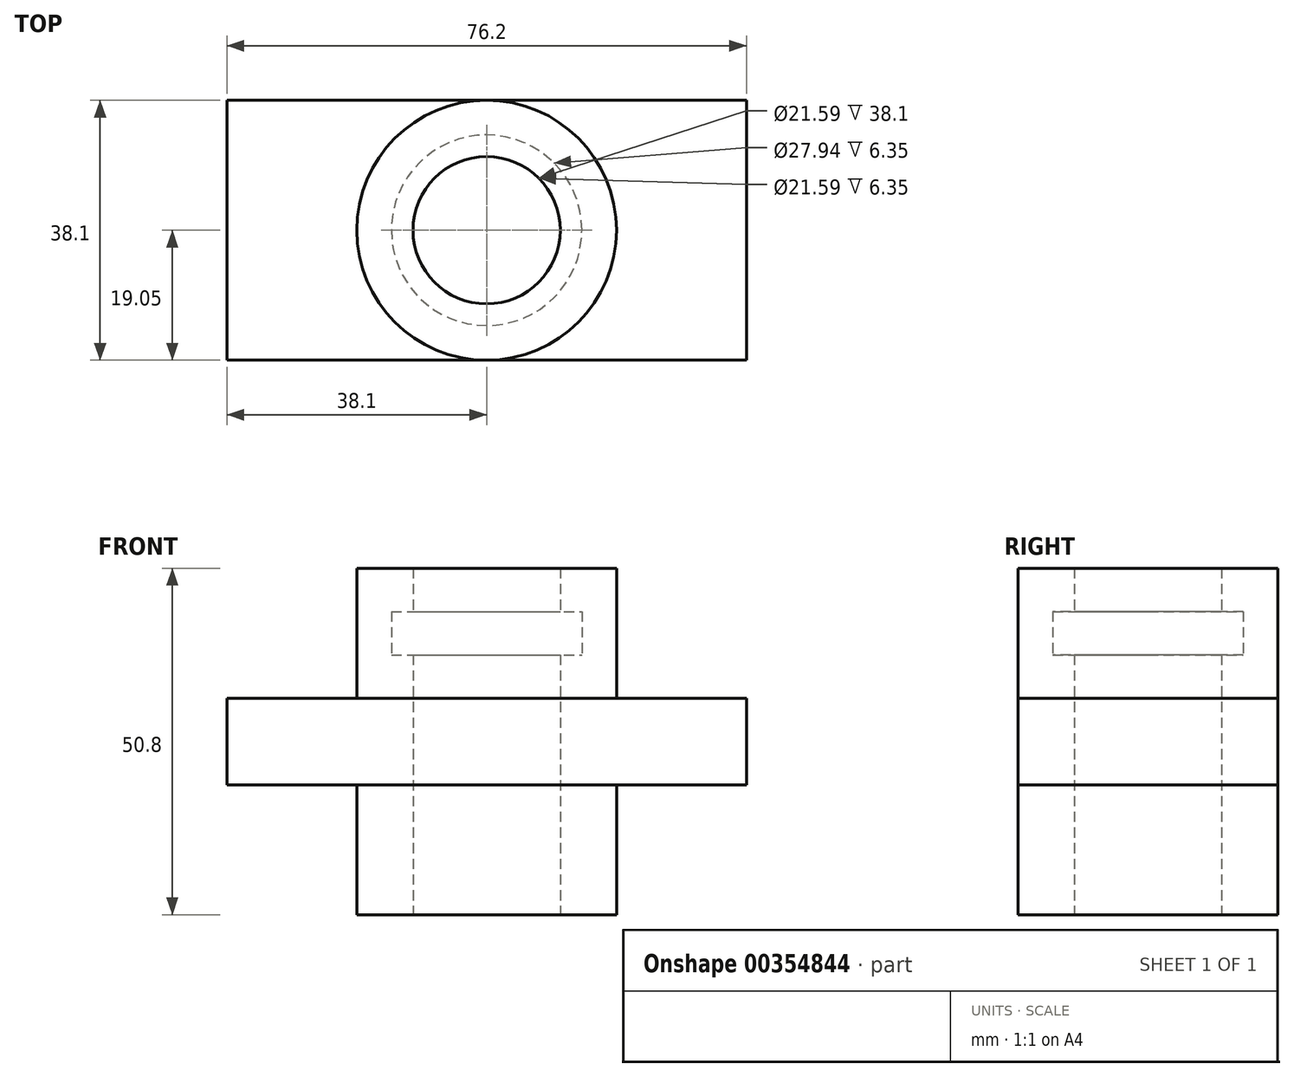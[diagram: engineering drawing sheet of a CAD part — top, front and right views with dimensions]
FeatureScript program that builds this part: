
annotation { "Feature Type Name" : "Feature", "Feature Type Description" : "" }
export const myFeature = defineFeature(function(context is Context, id is Id, definition is map)
    precondition{}
    {
        {
            var Q0;
            Q0=qCreatedBy(makeId("Front.planeOp"),FACE);
            var sketch = newSketch(context, id + "F0", { "sketchPlane" : qUnion([Q0])});
            skLineSegment(sketch, "E0", {"start": v(0, 0) * mm, "end": v(38.1, 0) * mm});
            skLineSegment(sketch, "E1", {"start": v(38.1, 0) * mm, "end": v(38.1, 12.7) * mm});
            skLineSegment(sketch, "E2", {"start": v(38.1, 12.7) * mm, "end": v(-38.1, 12.7) * mm});
            skLineSegment(sketch, "E3", {"start": v(-38.1, 12.7) * mm, "end": v(-38.1, 0) * mm});
            skLineSegment(sketch, "E4", {"start": v(-38.1, 0) * mm, "end": v(0, 0) * mm});
            skSolve(sketch);
        }
        {
            var Q0;
            Q0=makeQuery(id+"F0.imprint","IMPRINT",FACE,{"disambiguationData":[TD([[makeQuery(id+"F0.imprint","IMPRINT",EDGE,{"derivedFrom":sQuery(id+"F0.wireOp",EDGE,"E0")}),1.0]])]});
            extrude(context, id + "F1", {"entities" : qUnion([Q0]), "endBound" : BoundingType.SYMMETRIC, "depth" : 38.1 * mm});
        }
        {
            var Q0;
            Q0=qCreatedBy(makeId("Front.planeOp"),FACE);
            var sketch = newSketch(context, id + "F2", { "sketchPlane" : qUnion([Q0])});
            skLineSegment(sketch, "E5.0.0", {"start": v(-38.1, 12.7) * mm, "end": v(-38.1, 0) * mm});
            skLineSegment(sketch, "E5.0.1", {"start": v(-38.1, 0) * mm, "end": v(38.1, 0) * mm});
            skLineSegment(sketch, "E5.0.2", {"start": v(38.1, 0) * mm, "end": v(38.1, 12.7) * mm});
            skLineSegment(sketch, "E5.0.3", {"start": v(38.1, 12.7) * mm, "end": v(-38.1, 12.7) * mm});
            skLineSegment(sketch, "E6", {"start": v(0, 12.7) * mm, "end": v(-19.05, 12.7) * mm});
            skLineSegment(sketch, "E7", {"start": v(-19.05, 12.7) * mm, "end": v(-19.05, 31.75) * mm});
            skLineSegment(sketch, "E8", {"start": v(-19.05, 31.75) * mm, "end": v(-10.8, 31.75) * mm});
            skLineSegment(sketch, "E9", {"start": v(-10.8, 31.75) * mm, "end": v(-10.8, 25.4) * mm});
            skLineSegment(sketch, "E10", {"start": v(-10.8, 25.4) * mm, "end": v(-13.97, 25.4) * mm});
            skLineSegment(sketch, "E11", {"start": v(-13.97, 25.4) * mm, "end": v(-13.97, 19.05) * mm});
            skLineSegment(sketch, "E12", {"start": v(-13.97, 19.05) * mm, "end": v(-10.8, 19.05) * mm});
            skLineSegment(sketch, "E13", {"start": v(-10.8, 19.05) * mm, "end": v(-10.8, 12.7) * mm});
            skLineSegment(sketch, "E14", {"start": v(0, 12.7) * mm, "end": v(0, 18.62) * mm});
            skSolve(sketch);
        }
        {
            var Q0;
            {var subQ0=sQuery(id+"F2.wireOp",EDGE,"E7");Q0=makeQuery(id+"F2.imprint","IMPRINT",FACE,{"disambiguationData":[TD([[makeQuery(id+"F2.imprint","IMPRINT",EDGE,{"derivedFrom":subQ0}),-1.0]])]});}
            var Q1;
            Q1=sQuery(id+"F2.wireOp",EDGE,"E14");
            revolve(context, id + "F3", {"operationType" : NewBodyOperationType.ADD, "entities" : qUnion([Q0]), "axis" : qUnion([Q1]), "revolveType" : RevolveType.FULL});
        }
        {
            var Q0;
            Q0=makeQuery(id+"F3.boolean.opBoolean","SPLIT",FACE,{"disambiguationData":[TD([makeQuery(id+"F3.opRevolve","SWEPT_FACE",FACE,{"disambiguationData":[OSD([sQuery(id+"F2.wireOp",EDGE,"E13")])]})])],"derivedFrom":makeQuery(id+"F1.opExtrude","SWEPT_FACE",FACE,{"disambiguationData":[OSD([sQuery(id+"F0.wireOp",EDGE,"E2")])]})});
            extrude(context, id + "F4", {"entities" : qUnion([Q0]), "operationType" : NewBodyOperationType.REMOVE, "oppositeDirection" : true, "depth" : 25.4 * mm});
        }
        {
            var Q0;
            Q0=makeQuery(id+"F1.opExtrude","SWEPT_FACE",FACE,{"disambiguationData":[OSD([sQuery(id+"F0.wireOp",EDGE,"E0"),sQuery(id+"F0.wireOp",EDGE,"E4")])]});
            var sketch = newSketch(context, id + "F5", { "sketchPlane" : qUnion([Q0])});
            skCircle(sketch, "E15", {"center": v(0, 0) * mm, "radius": 19.05 * mm});
            skCircle(sketch, "E16.0", {"center": v(0, 0) * mm, "radius": 10.8 * mm});
            skSolve(sketch);
        }
        {
            var Q0;
            Q0=makeQuery(id+"F5.imprint","IMPRINT",FACE,{"disambiguationData":[TD([[makeQuery(id+"F5.imprint","IMPRINT",EDGE,{"derivedFrom":sQuery(id+"F5.wireOp",EDGE,"E16.0")}),-1.0]])]});
            extrude(context, id + "F6", {"entities" : qUnion([Q0]), "operationType" : NewBodyOperationType.ADD, "depth" : 19.05 * mm});
        }
    });
